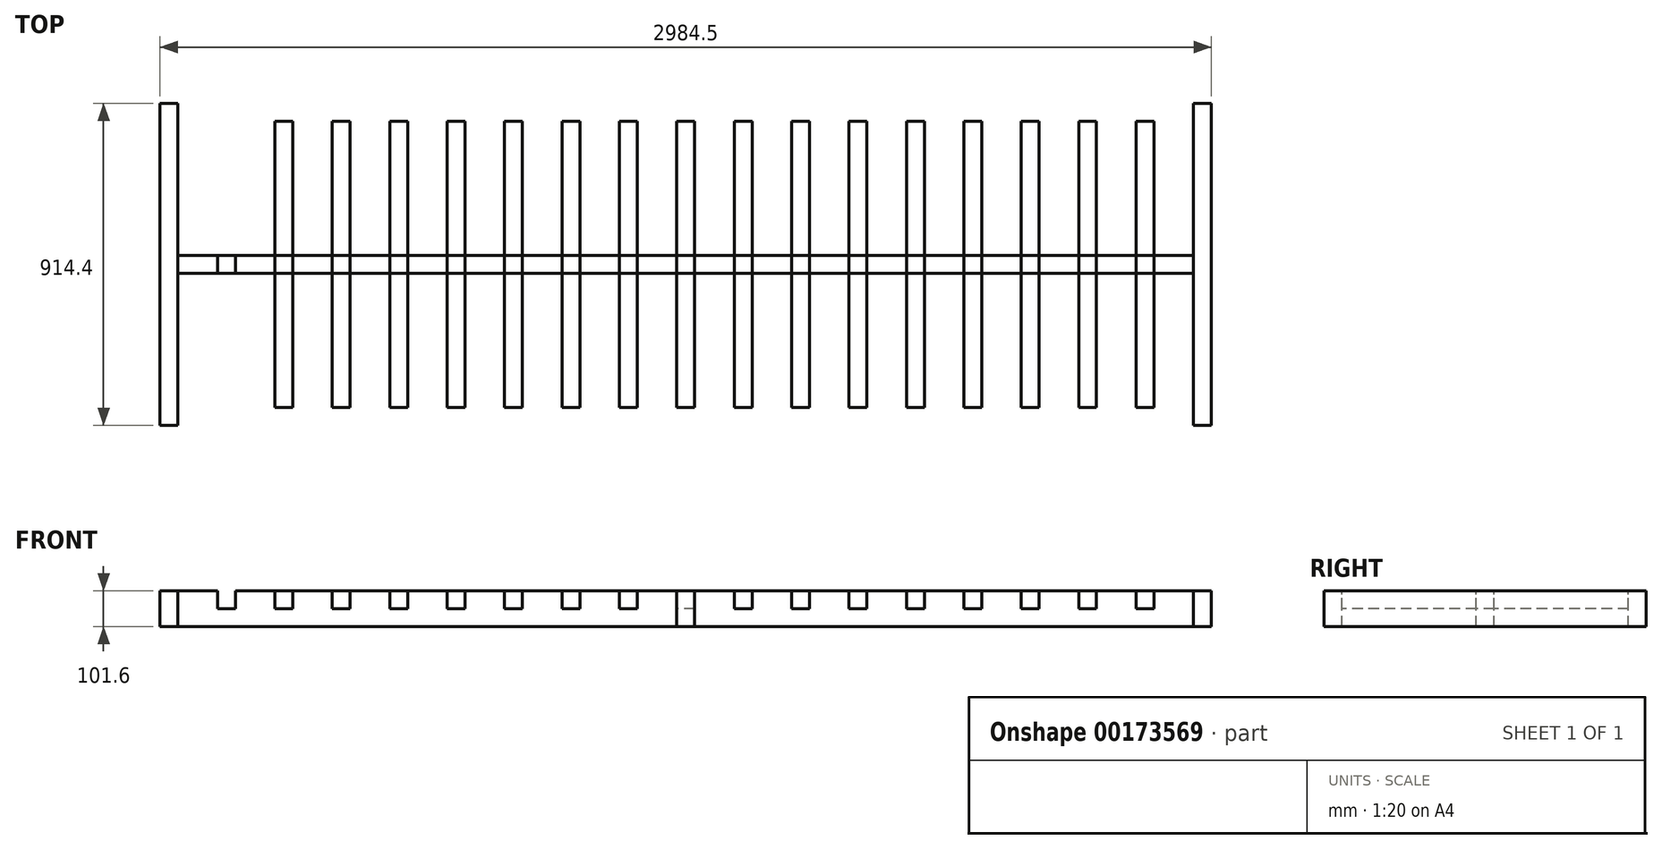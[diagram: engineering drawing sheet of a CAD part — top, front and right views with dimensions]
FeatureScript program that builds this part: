
annotation { "Feature Type Name" : "Feature", "Feature Type Description" : "" }
export const myFeature = defineFeature(function(context is Context, id is Id, definition is map)
    precondition{}
    {
        {
            var Q0;
            Q0=qCreatedBy(makeId("Top.planeOp"),FACE);
            var sketch = newSketch(context, id + "F0", { "sketchPlane" : qUnion([Q0])});
            skLineSegment(sketch, "E0.bottom", {"start": v(1492.25, 457.2) * mm, "end": v(-1492.25, 457.2) * mm});
            skLineSegment(sketch, "E0.top", {"start": v(1492.25, -457.2) * mm, "end": v(-1492.25, -457.2) * mm});
            skLineSegment(sketch, "E0.left", {"start": v(1492.25, 457.2) * mm, "end": v(1492.25, -457.2) * mm});
            skLineSegment(sketch, "E0.right", {"start": v(-1492.25, 457.2) * mm, "end": v(-1492.25, -457.2) * mm});
            skPoint(sketch, "E0.middle", {"position": v(0, 0) * mm});
            skLineSegment(sketch, "E1.0", {"start": v(1441.45, 406.4) * mm, "end": v(-1441.45, 406.4) * mm});
            skLineSegment(sketch, "E1.1", {"start": v(1441.45, 406.4) * mm, "end": v(1441.45, -406.4) * mm});
            skLineSegment(sketch, "E1.2", {"start": v(1441.45, -406.4) * mm, "end": v(-1441.45, -406.4) * mm});
            skLineSegment(sketch, "E1.3", {"start": v(-1441.45, 406.4) * mm, "end": v(-1441.45, -406.4) * mm});
            skLineSegment(sketch, "E2.bottom", {"start": v(1441.45, 25.4) * mm, "end": v(-1441.45, 25.4) * mm});
            skLineSegment(sketch, "E2.top", {"start": v(1441.45, -25.4) * mm, "end": v(-1441.45, -25.4) * mm});
            skLineSegment(sketch, "E2.left", {"start": v(1441.45, 25.4) * mm, "end": v(1441.45, -25.4) * mm});
            skLineSegment(sketch, "E2.right", {"start": v(-1441.45, 25.4) * mm, "end": v(-1441.45, -25.4) * mm});
            skLineSegment(sketch, "E3.bottom", {"start": v(-1329.18, 406.4) * mm, "end": v(-1278.38, 406.4) * mm});
            skLineSegment(sketch, "E3.top", {"start": v(-1329.18, -406.4) * mm, "end": v(-1278.38, -406.4) * mm});
            skLineSegment(sketch, "E3.left", {"start": v(-1329.18, 406.4) * mm, "end": v(-1329.18, -406.4) * mm});
            skLineSegment(sketch, "E3.right", {"start": v(-1278.38, 406.4) * mm, "end": v(-1278.38, -406.4) * mm});
            skLineSegment(sketch, "E4.1.0.0", {"start": v(-1115.4, 406.4) * mm, "end": v(-1115.4, -406.4) * mm});
            skLineSegment(sketch, "E4.1.0.1", {"start": v(-1166.2, 406.4) * mm, "end": v(-1166.2, -406.4) * mm});
            skLineSegment(sketch, "E4.2.0.0", {"start": v(-952.44, 406.4) * mm, "end": v(-952.44, -406.4) * mm});
            skLineSegment(sketch, "E4.2.0.1", {"start": v(-1003.24, 406.4) * mm, "end": v(-1003.24, -406.4) * mm});
            skLineSegment(sketch, "E4.direction1", {"start": v(-1278.38, -406.4) * mm, "end": v(-1115.4, -406.4) * mm, "construction": true});
            skLineSegment(sketch, "E5.0.3.0", {"start": v(-789.46, 406.4) * mm, "end": v(-789.46, -406.4) * mm});
            skLineSegment(sketch, "E5.3.3.0", {"start": v(-840.26, 406.4) * mm, "end": v(-840.26, -406.4) * mm});
            skLineSegment(sketch, "E5.0.4.0", {"start": v(-626.5, 406.4) * mm, "end": v(-626.5, -406.4) * mm});
            skLineSegment(sketch, "E5.3.4.0", {"start": v(-677.3, 406.4) * mm, "end": v(-677.3, -406.4) * mm});
            skLineSegment(sketch, "E5.0.5.0", {"start": v(-463.52, 406.4) * mm, "end": v(-463.52, -406.4) * mm});
            skLineSegment(sketch, "E5.3.5.0", {"start": v(-514.32, 406.4) * mm, "end": v(-514.32, -406.4) * mm});
            skLineSegment(sketch, "E5.0.6.0", {"start": v(-300.55, 406.4) * mm, "end": v(-300.55, -406.4) * mm});
            skLineSegment(sketch, "E5.3.6.0", {"start": v(-351.35, 406.4) * mm, "end": v(-351.35, -406.4) * mm});
            skLineSegment(sketch, "E5.0.7.0", {"start": v(-137.57, 406.4) * mm, "end": v(-137.57, -406.4) * mm});
            skLineSegment(sketch, "E5.3.7.0", {"start": v(-188.37, 406.4) * mm, "end": v(-188.37, -406.4) * mm});
            skLineSegment(sketch, "E5.0.8.0", {"start": v(25.4, 406.4) * mm, "end": v(25.4, -406.4) * mm});
            skLineSegment(sketch, "E5.3.8.0", {"start": v(-25.4, 406.4) * mm, "end": v(-25.4, -406.4) * mm});
            skLineSegment(sketch, "E5.0.9.0", {"start": v(188.37, 406.4) * mm, "end": v(188.37, -406.4) * mm});
            skLineSegment(sketch, "E5.3.9.0", {"start": v(137.57, 406.4) * mm, "end": v(137.57, -406.4) * mm});
            skLineSegment(sketch, "E5.0.10.0", {"start": v(351.35, 406.4) * mm, "end": v(351.35, -406.4) * mm});
            skLineSegment(sketch, "E5.3.10.0", {"start": v(300.55, 406.4) * mm, "end": v(300.55, -406.4) * mm});
            skLineSegment(sketch, "E5.0.11.0", {"start": v(514.32, 406.4) * mm, "end": v(514.32, -406.4) * mm});
            skLineSegment(sketch, "E5.3.11.0", {"start": v(463.52, 406.4) * mm, "end": v(463.52, -406.4) * mm});
            skLineSegment(sketch, "E6.0.12.0", {"start": v(677.3, 406.4) * mm, "end": v(677.3, -406.4) * mm});
            skLineSegment(sketch, "E6.3.12.0", {"start": v(626.5, 406.4) * mm, "end": v(626.5, -406.4) * mm});
            skLineSegment(sketch, "E6.0.13.0", {"start": v(840.26, 406.4) * mm, "end": v(840.26, -406.4) * mm});
            skLineSegment(sketch, "E6.3.13.0", {"start": v(789.46, 406.4) * mm, "end": v(789.46, -406.4) * mm});
            skLineSegment(sketch, "E7.0.14.0", {"start": v(1003.24, 406.4) * mm, "end": v(1003.24, -406.4) * mm});
            skLineSegment(sketch, "E7.3.14.0", {"start": v(952.44, 406.4) * mm, "end": v(952.44, -406.4) * mm});
            skLineSegment(sketch, "E7.0.15.0", {"start": v(1166.2, 406.4) * mm, "end": v(1166.2, -406.4) * mm});
            skLineSegment(sketch, "E7.3.15.0", {"start": v(1115.4, 406.4) * mm, "end": v(1115.4, -406.4) * mm});
            skLineSegment(sketch, "E8", {"start": v(-1441.45, 406.4) * mm, "end": v(-1441.45, 457.2) * mm});
            skLineSegment(sketch, "E9", {"start": v(-1441.45, -406.4) * mm, "end": v(-1441.45, -457.2) * mm});
            skLineSegment(sketch, "E10", {"start": v(1441.45, 406.4) * mm, "end": v(1441.45, 457.2) * mm});
            skLineSegment(sketch, "E11", {"start": v(1441.45, -406.4) * mm, "end": v(1441.45, -457.2) * mm});
            skLineSegment(sketch, "E12.0.16.0", {"start": v(1329.18, 406.4) * mm, "end": v(1329.18, -406.4) * mm});
            skLineSegment(sketch, "E12.3.16.0", {"start": v(1278.38, 406.4) * mm, "end": v(1278.38, -406.4) * mm});
            skSolve(sketch);
        }
        {
            var Q0;
            {var subQ0=sQuery(id+"F0.wireOp",EDGE,"E12.0.16.0");var subQ1=sQuery(id+"F0.wireOp",EDGE,"E1.0");var subQ2=makeQuery(id+"F0.imprint","INTERSECT",VERTEX,{"derivedFrom":[subQ1,subQ0]});Q0=makeQuery(id+"F0.imprint","IMPRINT",FACE,{"disambiguationData":[TD([[makeQuery(id+"F0.imprint","IMPRINT",EDGE,{"disambiguationData":[TD([[subQ2,-1.0]])],"derivedFrom":subQ1}),1.0]])]});}
            var Q1;
            {var subQ0=sQuery(id+"F0.wireOp",EDGE,"E12.0.16.0");var subQ1=sQuery(id+"F0.wireOp",EDGE,"E1.2");var subQ2=makeQuery(id+"F0.imprint","INTERSECT",VERTEX,{"derivedFrom":[subQ1,subQ0]});Q1=makeQuery(id+"F0.imprint","IMPRINT",FACE,{"disambiguationData":[TD([[makeQuery(id+"F0.imprint","IMPRINT",EDGE,{"disambiguationData":[TD([[subQ2,-1.0]])],"derivedFrom":subQ1}),-1.0]])]});}
            var Q2;
            {var subQ0=sQuery(id+"F0.wireOp",EDGE,"E7.0.15.0");var subQ1=sQuery(id+"F0.wireOp",EDGE,"E1.2");var subQ2=makeQuery(id+"F0.imprint","INTERSECT",VERTEX,{"derivedFrom":[subQ1,subQ0]});Q2=makeQuery(id+"F0.imprint","IMPRINT",FACE,{"disambiguationData":[TD([[makeQuery(id+"F0.imprint","IMPRINT",EDGE,{"disambiguationData":[TD([[subQ2,-1.0]])],"derivedFrom":subQ1}),-1.0]])]});}
            var Q3;
            {var subQ0=sQuery(id+"F0.wireOp",EDGE,"E7.0.15.0");var subQ1=sQuery(id+"F0.wireOp",EDGE,"E2.bottom");var subQ2=makeQuery(id+"F0.imprint","INTERSECT",VERTEX,{"derivedFrom":[subQ1,subQ0]});Q3=makeQuery(id+"F0.imprint","IMPRINT",FACE,{"disambiguationData":[TD([[makeQuery(id+"F0.imprint","IMPRINT",EDGE,{"disambiguationData":[TD([[subQ2,-1.0]])],"derivedFrom":subQ1}),1.0]])]});}
            var Q4;
            {var subQ0=sQuery(id+"F0.wireOp",EDGE,"E7.0.15.0");var subQ1=sQuery(id+"F0.wireOp",EDGE,"E1.0");var subQ2=makeQuery(id+"F0.imprint","INTERSECT",VERTEX,{"derivedFrom":[subQ1,subQ0]});Q4=makeQuery(id+"F0.imprint","IMPRINT",FACE,{"disambiguationData":[TD([[makeQuery(id+"F0.imprint","IMPRINT",EDGE,{"disambiguationData":[TD([[subQ2,-1.0]])],"derivedFrom":subQ1}),1.0]])]});}
            var Q5;
            {var subQ0=sQuery(id+"F0.wireOp",EDGE,"E7.0.14.0");var subQ1=sQuery(id+"F0.wireOp",EDGE,"E1.2");var subQ2=makeQuery(id+"F0.imprint","INTERSECT",VERTEX,{"derivedFrom":[subQ1,subQ0]});Q5=makeQuery(id+"F0.imprint","IMPRINT",FACE,{"disambiguationData":[TD([[makeQuery(id+"F0.imprint","IMPRINT",EDGE,{"disambiguationData":[TD([[subQ2,-1.0]])],"derivedFrom":subQ1}),-1.0]])]});}
            var Q6;
            {var subQ0=sQuery(id+"F0.wireOp",EDGE,"E7.0.14.0");var subQ1=sQuery(id+"F0.wireOp",EDGE,"E2.bottom");var subQ2=makeQuery(id+"F0.imprint","INTERSECT",VERTEX,{"derivedFrom":[subQ1,subQ0]});Q6=makeQuery(id+"F0.imprint","IMPRINT",FACE,{"disambiguationData":[TD([[makeQuery(id+"F0.imprint","IMPRINT",EDGE,{"disambiguationData":[TD([[subQ2,-1.0]])],"derivedFrom":subQ1}),1.0]])]});}
            var Q7;
            {var subQ0=sQuery(id+"F0.wireOp",EDGE,"E7.0.14.0");var subQ1=sQuery(id+"F0.wireOp",EDGE,"E1.0");var subQ2=makeQuery(id+"F0.imprint","INTERSECT",VERTEX,{"derivedFrom":[subQ1,subQ0]});Q7=makeQuery(id+"F0.imprint","IMPRINT",FACE,{"disambiguationData":[TD([[makeQuery(id+"F0.imprint","IMPRINT",EDGE,{"disambiguationData":[TD([[subQ2,-1.0]])],"derivedFrom":subQ1}),1.0]])]});}
            var Q8;
            {var subQ0=sQuery(id+"F0.wireOp",EDGE,"E6.0.12.0");var subQ1=sQuery(id+"F0.wireOp",EDGE,"E2.bottom");var subQ2=makeQuery(id+"F0.imprint","INTERSECT",VERTEX,{"derivedFrom":[subQ1,subQ0]});Q8=makeQuery(id+"F0.imprint","IMPRINT",FACE,{"disambiguationData":[TD([[makeQuery(id+"F0.imprint","IMPRINT",EDGE,{"disambiguationData":[TD([[subQ2,-1.0]])],"derivedFrom":subQ1}),1.0]])]});}
            var Q9;
            {var subQ0=sQuery(id+"F0.wireOp",EDGE,"E6.0.12.0");var subQ1=sQuery(id+"F0.wireOp",EDGE,"E1.0");var subQ2=makeQuery(id+"F0.imprint","INTERSECT",VERTEX,{"derivedFrom":[subQ1,subQ0]});Q9=makeQuery(id+"F0.imprint","IMPRINT",FACE,{"disambiguationData":[TD([[makeQuery(id+"F0.imprint","IMPRINT",EDGE,{"disambiguationData":[TD([[subQ2,-1.0]])],"derivedFrom":subQ1}),1.0]])]});}
            var Q10;
            {var subQ0=sQuery(id+"F0.wireOp",EDGE,"E6.0.12.0");var subQ1=sQuery(id+"F0.wireOp",EDGE,"E1.2");var subQ2=makeQuery(id+"F0.imprint","INTERSECT",VERTEX,{"derivedFrom":[subQ1,subQ0]});Q10=makeQuery(id+"F0.imprint","IMPRINT",FACE,{"disambiguationData":[TD([[makeQuery(id+"F0.imprint","IMPRINT",EDGE,{"disambiguationData":[TD([[subQ2,-1.0]])],"derivedFrom":subQ1}),-1.0]])]});}
            var Q11;
            {var subQ0=sQuery(id+"F0.wireOp",EDGE,"E5.0.11.0");var subQ1=sQuery(id+"F0.wireOp",EDGE,"E2.bottom");var subQ2=makeQuery(id+"F0.imprint","INTERSECT",VERTEX,{"derivedFrom":[subQ1,subQ0]});Q11=makeQuery(id+"F0.imprint","IMPRINT",FACE,{"disambiguationData":[TD([[makeQuery(id+"F0.imprint","IMPRINT",EDGE,{"disambiguationData":[TD([[subQ2,-1.0]])],"derivedFrom":subQ1}),1.0]])]});}
            var Q12;
            {var subQ0=sQuery(id+"F0.wireOp",EDGE,"E5.0.11.0");var subQ1=sQuery(id+"F0.wireOp",EDGE,"E1.0");var subQ2=makeQuery(id+"F0.imprint","INTERSECT",VERTEX,{"derivedFrom":[subQ1,subQ0]});Q12=makeQuery(id+"F0.imprint","IMPRINT",FACE,{"disambiguationData":[TD([[makeQuery(id+"F0.imprint","IMPRINT",EDGE,{"disambiguationData":[TD([[subQ2,-1.0]])],"derivedFrom":subQ1}),1.0]])]});}
            var Q13;
            {var subQ0=sQuery(id+"F0.wireOp",EDGE,"E5.0.11.0");var subQ1=sQuery(id+"F0.wireOp",EDGE,"E1.2");var subQ2=makeQuery(id+"F0.imprint","INTERSECT",VERTEX,{"derivedFrom":[subQ1,subQ0]});Q13=makeQuery(id+"F0.imprint","IMPRINT",FACE,{"disambiguationData":[TD([[makeQuery(id+"F0.imprint","IMPRINT",EDGE,{"disambiguationData":[TD([[subQ2,-1.0]])],"derivedFrom":subQ1}),-1.0]])]});}
            var Q14;
            {var subQ0=sQuery(id+"F0.wireOp",EDGE,"E5.0.10.0");var subQ1=sQuery(id+"F0.wireOp",EDGE,"E2.bottom");var subQ2=makeQuery(id+"F0.imprint","INTERSECT",VERTEX,{"derivedFrom":[subQ1,subQ0]});Q14=makeQuery(id+"F0.imprint","IMPRINT",FACE,{"disambiguationData":[TD([[makeQuery(id+"F0.imprint","IMPRINT",EDGE,{"disambiguationData":[TD([[subQ2,-1.0]])],"derivedFrom":subQ1}),1.0]])]});}
            var Q15;
            {var subQ0=sQuery(id+"F0.wireOp",EDGE,"E5.0.10.0");var subQ1=sQuery(id+"F0.wireOp",EDGE,"E1.2");var subQ2=makeQuery(id+"F0.imprint","INTERSECT",VERTEX,{"derivedFrom":[subQ1,subQ0]});Q15=makeQuery(id+"F0.imprint","IMPRINT",FACE,{"disambiguationData":[TD([[makeQuery(id+"F0.imprint","IMPRINT",EDGE,{"disambiguationData":[TD([[subQ2,-1.0]])],"derivedFrom":subQ1}),-1.0]])]});}
            var Q16;
            {var subQ0=sQuery(id+"F0.wireOp",EDGE,"E5.0.10.0");var subQ1=sQuery(id+"F0.wireOp",EDGE,"E1.0");var subQ2=makeQuery(id+"F0.imprint","INTERSECT",VERTEX,{"derivedFrom":[subQ1,subQ0]});Q16=makeQuery(id+"F0.imprint","IMPRINT",FACE,{"disambiguationData":[TD([[makeQuery(id+"F0.imprint","IMPRINT",EDGE,{"disambiguationData":[TD([[subQ2,-1.0]])],"derivedFrom":subQ1}),1.0]])]});}
            var Q17;
            {var subQ0=sQuery(id+"F0.wireOp",EDGE,"E5.0.9.0");var subQ1=sQuery(id+"F0.wireOp",EDGE,"E1.2");var subQ2=makeQuery(id+"F0.imprint","INTERSECT",VERTEX,{"derivedFrom":[subQ1,subQ0]});Q17=makeQuery(id+"F0.imprint","IMPRINT",FACE,{"disambiguationData":[TD([[makeQuery(id+"F0.imprint","IMPRINT",EDGE,{"disambiguationData":[TD([[subQ2,-1.0]])],"derivedFrom":subQ1}),-1.0]])]});}
            var Q18;
            {var subQ0=sQuery(id+"F0.wireOp",EDGE,"E5.0.9.0");var subQ1=sQuery(id+"F0.wireOp",EDGE,"E1.0");var subQ2=makeQuery(id+"F0.imprint","INTERSECT",VERTEX,{"derivedFrom":[subQ1,subQ0]});Q18=makeQuery(id+"F0.imprint","IMPRINT",FACE,{"disambiguationData":[TD([[makeQuery(id+"F0.imprint","IMPRINT",EDGE,{"disambiguationData":[TD([[subQ2,-1.0]])],"derivedFrom":subQ1}),1.0]])]});}
            var Q19;
            {var subQ0=sQuery(id+"F0.wireOp",EDGE,"E5.0.9.0");var subQ1=sQuery(id+"F0.wireOp",EDGE,"E2.bottom");var subQ2=makeQuery(id+"F0.imprint","INTERSECT",VERTEX,{"derivedFrom":[subQ1,subQ0]});Q19=makeQuery(id+"F0.imprint","IMPRINT",FACE,{"disambiguationData":[TD([[makeQuery(id+"F0.imprint","IMPRINT",EDGE,{"disambiguationData":[TD([[subQ2,-1.0]])],"derivedFrom":subQ1}),1.0]])]});}
            var Q20;
            {var subQ0=sQuery(id+"F0.wireOp",EDGE,"E5.0.8.0");var subQ1=sQuery(id+"F0.wireOp",EDGE,"E1.0");var subQ2=makeQuery(id+"F0.imprint","INTERSECT",VERTEX,{"derivedFrom":[subQ1,subQ0]});Q20=makeQuery(id+"F0.imprint","IMPRINT",FACE,{"disambiguationData":[TD([[makeQuery(id+"F0.imprint","IMPRINT",EDGE,{"disambiguationData":[TD([[subQ2,-1.0]])],"derivedFrom":subQ1}),1.0]])]});}
            var Q21;
            {var subQ0=sQuery(id+"F0.wireOp",EDGE,"E5.0.8.0");var subQ1=sQuery(id+"F0.wireOp",EDGE,"E1.2");var subQ2=makeQuery(id+"F0.imprint","INTERSECT",VERTEX,{"derivedFrom":[subQ1,subQ0]});Q21=makeQuery(id+"F0.imprint","IMPRINT",FACE,{"disambiguationData":[TD([[makeQuery(id+"F0.imprint","IMPRINT",EDGE,{"disambiguationData":[TD([[subQ2,-1.0]])],"derivedFrom":subQ1}),-1.0]])]});}
            var Q22;
            {var subQ0=sQuery(id+"F0.wireOp",EDGE,"E5.0.8.0");var subQ1=sQuery(id+"F0.wireOp",EDGE,"E2.bottom");var subQ2=makeQuery(id+"F0.imprint","INTERSECT",VERTEX,{"derivedFrom":[subQ1,subQ0]});Q22=makeQuery(id+"F0.imprint","IMPRINT",FACE,{"disambiguationData":[TD([[makeQuery(id+"F0.imprint","IMPRINT",EDGE,{"disambiguationData":[TD([[subQ2,-1.0]])],"derivedFrom":subQ1}),1.0]])]});}
            var Q23;
            {var subQ0=sQuery(id+"F0.wireOp",EDGE,"E5.0.7.0");var subQ1=sQuery(id+"F0.wireOp",EDGE,"E1.2");var subQ2=makeQuery(id+"F0.imprint","INTERSECT",VERTEX,{"derivedFrom":[subQ1,subQ0]});Q23=makeQuery(id+"F0.imprint","IMPRINT",FACE,{"disambiguationData":[TD([[makeQuery(id+"F0.imprint","IMPRINT",EDGE,{"disambiguationData":[TD([[subQ2,-1.0]])],"derivedFrom":subQ1}),-1.0]])]});}
            var Q24;
            {var subQ0=sQuery(id+"F0.wireOp",EDGE,"E5.0.7.0");var subQ1=sQuery(id+"F0.wireOp",EDGE,"E2.bottom");var subQ2=makeQuery(id+"F0.imprint","INTERSECT",VERTEX,{"derivedFrom":[subQ1,subQ0]});Q24=makeQuery(id+"F0.imprint","IMPRINT",FACE,{"disambiguationData":[TD([[makeQuery(id+"F0.imprint","IMPRINT",EDGE,{"disambiguationData":[TD([[subQ2,-1.0]])],"derivedFrom":subQ1}),1.0]])]});}
            var Q25;
            {var subQ0=sQuery(id+"F0.wireOp",EDGE,"E5.0.7.0");var subQ1=sQuery(id+"F0.wireOp",EDGE,"E1.0");var subQ2=makeQuery(id+"F0.imprint","INTERSECT",VERTEX,{"derivedFrom":[subQ1,subQ0]});Q25=makeQuery(id+"F0.imprint","IMPRINT",FACE,{"disambiguationData":[TD([[makeQuery(id+"F0.imprint","IMPRINT",EDGE,{"disambiguationData":[TD([[subQ2,-1.0]])],"derivedFrom":subQ1}),1.0]])]});}
            var Q26;
            {var subQ0=sQuery(id+"F0.wireOp",EDGE,"E5.0.5.0");var subQ1=sQuery(id+"F0.wireOp",EDGE,"E1.2");var subQ2=makeQuery(id+"F0.imprint","INTERSECT",VERTEX,{"derivedFrom":[subQ1,subQ0]});Q26=makeQuery(id+"F0.imprint","IMPRINT",FACE,{"disambiguationData":[TD([[makeQuery(id+"F0.imprint","IMPRINT",EDGE,{"disambiguationData":[TD([[subQ2,-1.0]])],"derivedFrom":subQ1}),-1.0]])]});}
            var Q27;
            {var subQ0=sQuery(id+"F0.wireOp",EDGE,"E5.0.5.0");var subQ1=sQuery(id+"F0.wireOp",EDGE,"E1.0");var subQ2=makeQuery(id+"F0.imprint","INTERSECT",VERTEX,{"derivedFrom":[subQ1,subQ0]});Q27=makeQuery(id+"F0.imprint","IMPRINT",FACE,{"disambiguationData":[TD([[makeQuery(id+"F0.imprint","IMPRINT",EDGE,{"disambiguationData":[TD([[subQ2,-1.0]])],"derivedFrom":subQ1}),1.0]])]});}
            var Q28;
            {var subQ0=sQuery(id+"F0.wireOp",EDGE,"E5.0.5.0");var subQ1=sQuery(id+"F0.wireOp",EDGE,"E2.bottom");var subQ2=makeQuery(id+"F0.imprint","INTERSECT",VERTEX,{"derivedFrom":[subQ1,subQ0]});Q28=makeQuery(id+"F0.imprint","IMPRINT",FACE,{"disambiguationData":[TD([[makeQuery(id+"F0.imprint","IMPRINT",EDGE,{"disambiguationData":[TD([[subQ2,-1.0]])],"derivedFrom":subQ1}),1.0]])]});}
            var Q29;
            {var subQ0=sQuery(id+"F0.wireOp",EDGE,"E5.0.3.0");var subQ1=sQuery(id+"F0.wireOp",EDGE,"E2.bottom");var subQ2=makeQuery(id+"F0.imprint","INTERSECT",VERTEX,{"derivedFrom":[subQ1,subQ0]});Q29=makeQuery(id+"F0.imprint","IMPRINT",FACE,{"disambiguationData":[TD([[makeQuery(id+"F0.imprint","IMPRINT",EDGE,{"disambiguationData":[TD([[subQ2,-1.0]])],"derivedFrom":subQ1}),1.0]])]});}
            var Q30;
            {var subQ0=sQuery(id+"F0.wireOp",EDGE,"E5.0.3.0");var subQ1=sQuery(id+"F0.wireOp",EDGE,"E1.2");var subQ2=makeQuery(id+"F0.imprint","INTERSECT",VERTEX,{"derivedFrom":[subQ1,subQ0]});Q30=makeQuery(id+"F0.imprint","IMPRINT",FACE,{"disambiguationData":[TD([[makeQuery(id+"F0.imprint","IMPRINT",EDGE,{"disambiguationData":[TD([[subQ2,-1.0]])],"derivedFrom":subQ1}),-1.0]])]});}
            var Q31;
            {var subQ0=sQuery(id+"F0.wireOp",EDGE,"E5.0.3.0");var subQ1=sQuery(id+"F0.wireOp",EDGE,"E1.0");var subQ2=makeQuery(id+"F0.imprint","INTERSECT",VERTEX,{"derivedFrom":[subQ1,subQ0]});Q31=makeQuery(id+"F0.imprint","IMPRINT",FACE,{"disambiguationData":[TD([[makeQuery(id+"F0.imprint","IMPRINT",EDGE,{"disambiguationData":[TD([[subQ2,-1.0]])],"derivedFrom":subQ1}),1.0]])]});}
            var Q32;
            {var subQ0=sQuery(id+"F0.wireOp",EDGE,"E4.2.0.0");var subQ1=sQuery(id+"F0.wireOp",EDGE,"E1.2");var subQ2=makeQuery(id+"F0.imprint","INTERSECT",VERTEX,{"derivedFrom":[subQ1,subQ0]});Q32=makeQuery(id+"F0.imprint","IMPRINT",FACE,{"disambiguationData":[TD([[makeQuery(id+"F0.imprint","IMPRINT",EDGE,{"disambiguationData":[TD([[subQ2,-1.0]])],"derivedFrom":subQ1}),-1.0]])]});}
            var Q33;
            {var subQ0=sQuery(id+"F0.wireOp",EDGE,"E4.2.0.0");var subQ1=sQuery(id+"F0.wireOp",EDGE,"E1.0");var subQ2=makeQuery(id+"F0.imprint","INTERSECT",VERTEX,{"derivedFrom":[subQ1,subQ0]});Q33=makeQuery(id+"F0.imprint","IMPRINT",FACE,{"disambiguationData":[TD([[makeQuery(id+"F0.imprint","IMPRINT",EDGE,{"disambiguationData":[TD([[subQ2,-1.0]])],"derivedFrom":subQ1}),1.0]])]});}
            var Q34;
            {var subQ0=sQuery(id+"F0.wireOp",EDGE,"E4.2.0.0");var subQ1=sQuery(id+"F0.wireOp",EDGE,"E2.bottom");var subQ2=makeQuery(id+"F0.imprint","INTERSECT",VERTEX,{"derivedFrom":[subQ1,subQ0]});Q34=makeQuery(id+"F0.imprint","IMPRINT",FACE,{"disambiguationData":[TD([[makeQuery(id+"F0.imprint","IMPRINT",EDGE,{"disambiguationData":[TD([[subQ2,-1.0]])],"derivedFrom":subQ1}),1.0]])]});}
            var Q35;
            {var subQ0=sQuery(id+"F0.wireOp",EDGE,"E4.1.0.0");var subQ1=sQuery(id+"F0.wireOp",EDGE,"E1.2");var subQ2=makeQuery(id+"F0.imprint","INTERSECT",VERTEX,{"derivedFrom":[subQ1,subQ0]});Q35=makeQuery(id+"F0.imprint","IMPRINT",FACE,{"disambiguationData":[TD([[makeQuery(id+"F0.imprint","IMPRINT",EDGE,{"disambiguationData":[TD([[subQ2,-1.0]])],"derivedFrom":subQ1}),-1.0]])]});}
            var Q36;
            {var subQ0=sQuery(id+"F0.wireOp",EDGE,"E12.0.16.0");var subQ1=sQuery(id+"F0.wireOp",EDGE,"E2.bottom");var subQ2=makeQuery(id+"F0.imprint","INTERSECT",VERTEX,{"derivedFrom":[subQ1,subQ0]});Q36=makeQuery(id+"F0.imprint","IMPRINT",FACE,{"disambiguationData":[TD([[makeQuery(id+"F0.imprint","IMPRINT",EDGE,{"disambiguationData":[TD([[subQ2,-1.0]])],"derivedFrom":subQ1}),1.0]])]});}
            var Q37;
            {var subQ5=sQuery(id+"F0.wireOp",EDGE,"E3.top");Q37=makeQuery(id+"F0.imprint","IMPRINT",FACE,{"disambiguationData":[TD([[makeQuery(id+"F0.imprint","IMPRINT",EDGE,{"derivedFrom":subQ5}),1.0]])]});}
            var Q38;
            {var subQ0=sQuery(id+"F0.wireOp",EDGE,"E3.right");var subQ1=sQuery(id+"F0.wireOp",EDGE,"E2.bottom");var subQ2=makeQuery(id+"F0.imprint","INTERSECT",VERTEX,{"derivedFrom":[subQ1,subQ0]});Q38=makeQuery(id+"F0.imprint","IMPRINT",FACE,{"disambiguationData":[TD([[makeQuery(id+"F0.imprint","IMPRINT",EDGE,{"disambiguationData":[TD([[subQ2,-1.0]])],"derivedFrom":subQ1}),1.0]])]});}
            var Q39;
            {var subQ5=sQuery(id+"F0.wireOp",EDGE,"E3.bottom");Q39=makeQuery(id+"F0.imprint","IMPRINT",FACE,{"disambiguationData":[TD([[makeQuery(id+"F0.imprint","IMPRINT",EDGE,{"derivedFrom":subQ5}),-1.0]])]});}
            var Q40;
            {var subQ0=sQuery(id+"F0.wireOp",EDGE,"E5.0.6.0");var subQ1=sQuery(id+"F0.wireOp",EDGE,"E1.2");var subQ2=makeQuery(id+"F0.imprint","INTERSECT",VERTEX,{"derivedFrom":[subQ1,subQ0]});Q40=makeQuery(id+"F0.imprint","IMPRINT",FACE,{"disambiguationData":[TD([[makeQuery(id+"F0.imprint","IMPRINT",EDGE,{"disambiguationData":[TD([[subQ2,-1.0]])],"derivedFrom":subQ1}),-1.0]])]});}
            var Q41;
            {var subQ0=sQuery(id+"F0.wireOp",EDGE,"E5.0.6.0");var subQ1=sQuery(id+"F0.wireOp",EDGE,"E2.bottom");var subQ2=makeQuery(id+"F0.imprint","INTERSECT",VERTEX,{"derivedFrom":[subQ1,subQ0]});Q41=makeQuery(id+"F0.imprint","IMPRINT",FACE,{"disambiguationData":[TD([[makeQuery(id+"F0.imprint","IMPRINT",EDGE,{"disambiguationData":[TD([[subQ2,-1.0]])],"derivedFrom":subQ1}),1.0]])]});}
            var Q42;
            {var subQ0=sQuery(id+"F0.wireOp",EDGE,"E5.0.6.0");var subQ1=sQuery(id+"F0.wireOp",EDGE,"E1.0");var subQ2=makeQuery(id+"F0.imprint","INTERSECT",VERTEX,{"derivedFrom":[subQ1,subQ0]});Q42=makeQuery(id+"F0.imprint","IMPRINT",FACE,{"disambiguationData":[TD([[makeQuery(id+"F0.imprint","IMPRINT",EDGE,{"disambiguationData":[TD([[subQ2,-1.0]])],"derivedFrom":subQ1}),1.0]])]});}
            var Q43;
            {var subQ0=sQuery(id+"F0.wireOp",EDGE,"E5.0.4.0");var subQ1=sQuery(id+"F0.wireOp",EDGE,"E1.2");var subQ2=makeQuery(id+"F0.imprint","INTERSECT",VERTEX,{"derivedFrom":[subQ1,subQ0]});Q43=makeQuery(id+"F0.imprint","IMPRINT",FACE,{"disambiguationData":[TD([[makeQuery(id+"F0.imprint","IMPRINT",EDGE,{"disambiguationData":[TD([[subQ2,-1.0]])],"derivedFrom":subQ1}),-1.0]])]});}
            var Q44;
            {var subQ0=sQuery(id+"F0.wireOp",EDGE,"E5.0.4.0");var subQ1=sQuery(id+"F0.wireOp",EDGE,"E1.0");var subQ2=makeQuery(id+"F0.imprint","INTERSECT",VERTEX,{"derivedFrom":[subQ1,subQ0]});Q44=makeQuery(id+"F0.imprint","IMPRINT",FACE,{"disambiguationData":[TD([[makeQuery(id+"F0.imprint","IMPRINT",EDGE,{"disambiguationData":[TD([[subQ2,-1.0]])],"derivedFrom":subQ1}),1.0]])]});}
            var Q45;
            {var subQ0=sQuery(id+"F0.wireOp",EDGE,"E5.0.4.0");var subQ1=sQuery(id+"F0.wireOp",EDGE,"E2.bottom");var subQ2=makeQuery(id+"F0.imprint","INTERSECT",VERTEX,{"derivedFrom":[subQ1,subQ0]});Q45=makeQuery(id+"F0.imprint","IMPRINT",FACE,{"disambiguationData":[TD([[makeQuery(id+"F0.imprint","IMPRINT",EDGE,{"disambiguationData":[TD([[subQ2,-1.0]])],"derivedFrom":subQ1}),1.0]])]});}
            var Q46;
            {var subQ0=sQuery(id+"F0.wireOp",EDGE,"E6.0.13.0");var subQ1=sQuery(id+"F0.wireOp",EDGE,"E1.2");var subQ2=makeQuery(id+"F0.imprint","INTERSECT",VERTEX,{"derivedFrom":[subQ1,subQ0]});Q46=makeQuery(id+"F0.imprint","IMPRINT",FACE,{"disambiguationData":[TD([[makeQuery(id+"F0.imprint","IMPRINT",EDGE,{"disambiguationData":[TD([[subQ2,-1.0]])],"derivedFrom":subQ1}),-1.0]])]});}
            var Q47;
            {var subQ0=sQuery(id+"F0.wireOp",EDGE,"E6.0.13.0");var subQ1=sQuery(id+"F0.wireOp",EDGE,"E1.0");var subQ2=makeQuery(id+"F0.imprint","INTERSECT",VERTEX,{"derivedFrom":[subQ1,subQ0]});Q47=makeQuery(id+"F0.imprint","IMPRINT",FACE,{"disambiguationData":[TD([[makeQuery(id+"F0.imprint","IMPRINT",EDGE,{"disambiguationData":[TD([[subQ2,-1.0]])],"derivedFrom":subQ1}),1.0]])]});}
            var Q48;
            {var subQ0=sQuery(id+"F0.wireOp",EDGE,"E6.0.13.0");var subQ1=sQuery(id+"F0.wireOp",EDGE,"E2.bottom");var subQ2=makeQuery(id+"F0.imprint","INTERSECT",VERTEX,{"derivedFrom":[subQ1,subQ0]});Q48=makeQuery(id+"F0.imprint","IMPRINT",FACE,{"disambiguationData":[TD([[makeQuery(id+"F0.imprint","IMPRINT",EDGE,{"disambiguationData":[TD([[subQ2,-1.0]])],"derivedFrom":subQ1}),1.0]])]});}
            var Q49;
            {var subQ0=sQuery(id+"F0.wireOp",EDGE,"E4.1.0.0");var subQ1=sQuery(id+"F0.wireOp",EDGE,"E1.0");var subQ2=makeQuery(id+"F0.imprint","INTERSECT",VERTEX,{"derivedFrom":[subQ1,subQ0]});Q49=makeQuery(id+"F0.imprint","IMPRINT",FACE,{"disambiguationData":[TD([[makeQuery(id+"F0.imprint","IMPRINT",EDGE,{"disambiguationData":[TD([[subQ2,-1.0]])],"derivedFrom":subQ1}),1.0]])]});}
            var Q50;
            {var subQ0=sQuery(id+"F0.wireOp",EDGE,"E4.1.0.0");var subQ1=sQuery(id+"F0.wireOp",EDGE,"E2.bottom");var subQ2=makeQuery(id+"F0.imprint","INTERSECT",VERTEX,{"derivedFrom":[subQ1,subQ0]});Q50=makeQuery(id+"F0.imprint","IMPRINT",FACE,{"disambiguationData":[TD([[makeQuery(id+"F0.imprint","IMPRINT",EDGE,{"disambiguationData":[TD([[subQ2,-1.0]])],"derivedFrom":subQ1}),1.0]])]});}
            extrude(context, id + "F1", {"entities" : qUnion([Q0, Q1, Q2, Q3, Q4, Q5, Q6, Q7, Q8, Q9, Q10, Q11, Q12, Q13, Q14, Q15, Q16, Q17, Q18, Q19, Q20, Q21, Q22, Q23, Q24, Q25, Q26, Q27, Q28, Q29, Q30, Q31, Q32, Q33, Q34, Q35, Q36, Q37, Q38, Q39, Q40, Q41, Q42, Q43, Q44, Q45, Q46, Q47, Q48, Q49, Q50]), "oppositeDirection" : true, "depth" : 50.8 * mm});
        }
        {
            var Q0;
            {var subQ0=sQuery(id+"F0.wireOp",EDGE,"E5.0.8.0");var subQ1=sQuery(id+"F0.wireOp",EDGE,"E1.0");var subQ2=makeQuery(id+"F0.imprint","INTERSECT",VERTEX,{"derivedFrom":[subQ1,subQ0]});Q0=makeQuery(id+"F0.imprint","IMPRINT",FACE,{"disambiguationData":[TD([[makeQuery(id+"F0.imprint","IMPRINT",EDGE,{"disambiguationData":[TD([[subQ2,-1.0]])],"derivedFrom":subQ1}),1.0]])]});}
            var Q1;
            {var subQ0=sQuery(id+"F0.wireOp",EDGE,"E5.0.8.0");var subQ1=sQuery(id+"F0.wireOp",EDGE,"E1.2");var subQ2=makeQuery(id+"F0.imprint","INTERSECT",VERTEX,{"derivedFrom":[subQ1,subQ0]});Q1=makeQuery(id+"F0.imprint","IMPRINT",FACE,{"disambiguationData":[TD([[makeQuery(id+"F0.imprint","IMPRINT",EDGE,{"disambiguationData":[TD([[subQ2,-1.0]])],"derivedFrom":subQ1}),-1.0]])]});}
            extrude(context, id + "F2", {"entities" : qUnion([Q0, Q1]), "operationType" : NewBodyOperationType.ADD, "oppositeDirection" : true, "depth" : 101.6 * mm});
        }
        {
            var Q0;
            {var subQ4=sQuery(id+"F0.wireOp",EDGE,"E0.right");Q0=makeQuery(id+"F0.imprint","IMPRINT",FACE,{"disambiguationData":[TD([[makeQuery(id+"F0.imprint","IMPRINT",EDGE,{"derivedFrom":subQ4}),1.0]])]});}
            var Q1;
            {var subQ3=sQuery(id+"F0.wireOp",EDGE,"E0.left");Q1=makeQuery(id+"F0.imprint","IMPRINT",FACE,{"disambiguationData":[TD([[makeQuery(id+"F0.imprint","IMPRINT",EDGE,{"derivedFrom":subQ3}),-1.0]])]});}
            extrude(context, id + "F3", {"entities" : qUnion([Q0, Q1]), "oppositeDirection" : true, "depth" : 101.6 * mm});
        }
        {
            var Q0;
            {var subQ0=sQuery(id+"F0.wireOp",EDGE,"E2.left");Q0=makeQuery(id+"F0.imprint","IMPRINT",FACE,{"disambiguationData":[TD([[makeQuery(id+"F0.imprint","IMPRINT",EDGE,{"derivedFrom":subQ0}),-1.0]])]});}
            var Q1;
            {var subQ0=sQuery(id+"F0.wireOp",EDGE,"f316c000-d505-4a66-956d-6f149d2779e3.0.17.0");var subQ1=sQuery(id+"F0.wireOp",EDGE,"E2.bottom");var subQ2=makeQuery(id+"F0.imprint","INTERSECT",VERTEX,{"derivedFrom":[subQ1,subQ0]});Q1=makeQuery(id+"F0.imprint","IMPRINT",FACE,{"disambiguationData":[TD([[makeQuery(id+"F0.imprint","IMPRINT",EDGE,{"disambiguationData":[TD([[subQ2,-1.0]])],"derivedFrom":subQ1}),1.0]])]});}
            var Q2;
            {var subQ0=sQuery(id+"F0.wireOp",EDGE,"f316c000-d505-4a66-956d-6f149d2779e3.3.17.0");var subQ1=sQuery(id+"F0.wireOp",EDGE,"E2.bottom");var subQ2=makeQuery(id+"F0.imprint","INTERSECT",VERTEX,{"derivedFrom":[subQ1,subQ0]});Q2=makeQuery(id+"F0.imprint","IMPRINT",FACE,{"disambiguationData":[TD([[makeQuery(id+"F0.imprint","IMPRINT",EDGE,{"disambiguationData":[TD([[subQ2,-1.0]])],"derivedFrom":subQ1}),1.0]])]});}
            var Q3;
            {var subQ0=sQuery(id+"F0.wireOp",EDGE,"f316c000-d505-4a66-956d-6f149d2779e3.0.16.0");var subQ1=sQuery(id+"F0.wireOp",EDGE,"E2.bottom");var subQ2=makeQuery(id+"F0.imprint","INTERSECT",VERTEX,{"derivedFrom":[subQ1,subQ0]});Q3=makeQuery(id+"F0.imprint","IMPRINT",FACE,{"disambiguationData":[TD([[makeQuery(id+"F0.imprint","IMPRINT",EDGE,{"disambiguationData":[TD([[subQ2,-1.0]])],"derivedFrom":subQ1}),1.0]])]});}
            var Q4;
            {var subQ0=sQuery(id+"F0.wireOp",EDGE,"f316c000-d505-4a66-956d-6f149d2779e3.3.16.0");var subQ1=sQuery(id+"F0.wireOp",EDGE,"E2.bottom");var subQ2=makeQuery(id+"F0.imprint","INTERSECT",VERTEX,{"derivedFrom":[subQ1,subQ0]});Q4=makeQuery(id+"F0.imprint","IMPRINT",FACE,{"disambiguationData":[TD([[makeQuery(id+"F0.imprint","IMPRINT",EDGE,{"disambiguationData":[TD([[subQ2,-1.0]])],"derivedFrom":subQ1}),1.0]])]});}
            var Q5;
            {var subQ0=sQuery(id+"F0.wireOp",EDGE,"E7.0.15.0");var subQ1=sQuery(id+"F0.wireOp",EDGE,"E2.bottom");var subQ2=makeQuery(id+"F0.imprint","INTERSECT",VERTEX,{"derivedFrom":[subQ1,subQ0]});Q5=makeQuery(id+"F0.imprint","IMPRINT",FACE,{"disambiguationData":[TD([[makeQuery(id+"F0.imprint","IMPRINT",EDGE,{"disambiguationData":[TD([[subQ2,-1.0]])],"derivedFrom":subQ1}),1.0]])]});}
            var Q6;
            {var subQ0=sQuery(id+"F0.wireOp",EDGE,"E7.0.14.0");var subQ1=sQuery(id+"F0.wireOp",EDGE,"E2.bottom");var subQ2=makeQuery(id+"F0.imprint","INTERSECT",VERTEX,{"derivedFrom":[subQ1,subQ0]});Q6=makeQuery(id+"F0.imprint","IMPRINT",FACE,{"disambiguationData":[TD([[makeQuery(id+"F0.imprint","IMPRINT",EDGE,{"disambiguationData":[TD([[subQ2,-1.0]])],"derivedFrom":subQ1}),1.0]])]});}
            var Q7;
            {var subQ0=sQuery(id+"F0.wireOp",EDGE,"E7.3.15.0");var subQ1=sQuery(id+"F0.wireOp",EDGE,"E2.bottom");var subQ2=makeQuery(id+"F0.imprint","INTERSECT",VERTEX,{"derivedFrom":[subQ1,subQ0]});Q7=makeQuery(id+"F0.imprint","IMPRINT",FACE,{"disambiguationData":[TD([[makeQuery(id+"F0.imprint","IMPRINT",EDGE,{"disambiguationData":[TD([[subQ2,-1.0]])],"derivedFrom":subQ1}),1.0]])]});}
            var Q8;
            {var subQ0=sQuery(id+"F0.wireOp",EDGE,"E7.3.14.0");var subQ1=sQuery(id+"F0.wireOp",EDGE,"E2.bottom");var subQ2=makeQuery(id+"F0.imprint","INTERSECT",VERTEX,{"derivedFrom":[subQ1,subQ0]});Q8=makeQuery(id+"F0.imprint","IMPRINT",FACE,{"disambiguationData":[TD([[makeQuery(id+"F0.imprint","IMPRINT",EDGE,{"disambiguationData":[TD([[subQ2,-1.0]])],"derivedFrom":subQ1}),1.0]])]});}
            var Q9;
            {var subQ0=sQuery(id+"F0.wireOp",EDGE,"E6.0.13.0");var subQ1=sQuery(id+"F0.wireOp",EDGE,"E2.bottom");var subQ2=makeQuery(id+"F0.imprint","INTERSECT",VERTEX,{"derivedFrom":[subQ1,subQ0]});Q9=makeQuery(id+"F0.imprint","IMPRINT",FACE,{"disambiguationData":[TD([[makeQuery(id+"F0.imprint","IMPRINT",EDGE,{"disambiguationData":[TD([[subQ2,-1.0]])],"derivedFrom":subQ1}),1.0]])]});}
            var Q10;
            {var subQ0=sQuery(id+"F0.wireOp",EDGE,"E6.3.12.0");var subQ1=sQuery(id+"F0.wireOp",EDGE,"E2.bottom");var subQ2=makeQuery(id+"F0.imprint","INTERSECT",VERTEX,{"derivedFrom":[subQ1,subQ0]});Q10=makeQuery(id+"F0.imprint","IMPRINT",FACE,{"disambiguationData":[TD([[makeQuery(id+"F0.imprint","IMPRINT",EDGE,{"disambiguationData":[TD([[subQ2,-1.0]])],"derivedFrom":subQ1}),1.0]])]});}
            var Q11;
            {var subQ0=sQuery(id+"F0.wireOp",EDGE,"E5.0.6.0");var subQ1=sQuery(id+"F0.wireOp",EDGE,"E2.bottom");var subQ2=makeQuery(id+"F0.imprint","INTERSECT",VERTEX,{"derivedFrom":[subQ1,subQ0]});Q11=makeQuery(id+"F0.imprint","IMPRINT",FACE,{"disambiguationData":[TD([[makeQuery(id+"F0.imprint","IMPRINT",EDGE,{"disambiguationData":[TD([[subQ2,-1.0]])],"derivedFrom":subQ1}),1.0]])]});}
            var Q12;
            {var subQ0=sQuery(id+"F0.wireOp",EDGE,"E5.0.10.0");var subQ1=sQuery(id+"F0.wireOp",EDGE,"E2.bottom");var subQ2=makeQuery(id+"F0.imprint","INTERSECT",VERTEX,{"derivedFrom":[subQ1,subQ0]});Q12=makeQuery(id+"F0.imprint","IMPRINT",FACE,{"disambiguationData":[TD([[makeQuery(id+"F0.imprint","IMPRINT",EDGE,{"disambiguationData":[TD([[subQ2,-1.0]])],"derivedFrom":subQ1}),1.0]])]});}
            var Q13;
            {var subQ0=sQuery(id+"F0.wireOp",EDGE,"E5.3.11.0");var subQ1=sQuery(id+"F0.wireOp",EDGE,"E2.bottom");var subQ2=makeQuery(id+"F0.imprint","INTERSECT",VERTEX,{"derivedFrom":[subQ1,subQ0]});Q13=makeQuery(id+"F0.imprint","IMPRINT",FACE,{"disambiguationData":[TD([[makeQuery(id+"F0.imprint","IMPRINT",EDGE,{"disambiguationData":[TD([[subQ2,-1.0]])],"derivedFrom":subQ1}),1.0]])]});}
            var Q14;
            {var subQ0=sQuery(id+"F0.wireOp",EDGE,"E6.0.12.0");var subQ1=sQuery(id+"F0.wireOp",EDGE,"E2.bottom");var subQ2=makeQuery(id+"F0.imprint","INTERSECT",VERTEX,{"derivedFrom":[subQ1,subQ0]});Q14=makeQuery(id+"F0.imprint","IMPRINT",FACE,{"disambiguationData":[TD([[makeQuery(id+"F0.imprint","IMPRINT",EDGE,{"disambiguationData":[TD([[subQ2,-1.0]])],"derivedFrom":subQ1}),1.0]])]});}
            var Q15;
            {var subQ0=sQuery(id+"F0.wireOp",EDGE,"E5.3.7.0");var subQ1=sQuery(id+"F0.wireOp",EDGE,"E2.bottom");var subQ2=makeQuery(id+"F0.imprint","INTERSECT",VERTEX,{"derivedFrom":[subQ1,subQ0]});Q15=makeQuery(id+"F0.imprint","IMPRINT",FACE,{"disambiguationData":[TD([[makeQuery(id+"F0.imprint","IMPRINT",EDGE,{"disambiguationData":[TD([[subQ2,-1.0]])],"derivedFrom":subQ1}),1.0]])]});}
            var Q16;
            {var subQ0=sQuery(id+"F0.wireOp",EDGE,"E5.3.3.0");var subQ1=sQuery(id+"F0.wireOp",EDGE,"E2.bottom");var subQ2=makeQuery(id+"F0.imprint","INTERSECT",VERTEX,{"derivedFrom":[subQ1,subQ0]});Q16=makeQuery(id+"F0.imprint","IMPRINT",FACE,{"disambiguationData":[TD([[makeQuery(id+"F0.imprint","IMPRINT",EDGE,{"disambiguationData":[TD([[subQ2,-1.0]])],"derivedFrom":subQ1}),1.0]])]});}
            var Q17;
            {var subQ0=sQuery(id+"F0.wireOp",EDGE,"E4.2.0.0");var subQ1=sQuery(id+"F0.wireOp",EDGE,"E2.bottom");var subQ2=makeQuery(id+"F0.imprint","INTERSECT",VERTEX,{"derivedFrom":[subQ1,subQ0]});Q17=makeQuery(id+"F0.imprint","IMPRINT",FACE,{"disambiguationData":[TD([[makeQuery(id+"F0.imprint","IMPRINT",EDGE,{"disambiguationData":[TD([[subQ2,-1.0]])],"derivedFrom":subQ1}),1.0]])]});}
            var Q18;
            {var subQ0=sQuery(id+"F0.wireOp",EDGE,"E4.1.0.1");var subQ1=sQuery(id+"F0.wireOp",EDGE,"E2.bottom");var subQ2=makeQuery(id+"F0.imprint","INTERSECT",VERTEX,{"derivedFrom":[subQ1,subQ0]});Q18=makeQuery(id+"F0.imprint","IMPRINT",FACE,{"disambiguationData":[TD([[makeQuery(id+"F0.imprint","IMPRINT",EDGE,{"disambiguationData":[TD([[subQ2,-1.0]])],"derivedFrom":subQ1}),1.0]])]});}
            var Q19;
            {var subQ0=sQuery(id+"F0.wireOp",EDGE,"E5.0.7.0");var subQ1=sQuery(id+"F0.wireOp",EDGE,"E2.bottom");var subQ2=makeQuery(id+"F0.imprint","INTERSECT",VERTEX,{"derivedFrom":[subQ1,subQ0]});Q19=makeQuery(id+"F0.imprint","IMPRINT",FACE,{"disambiguationData":[TD([[makeQuery(id+"F0.imprint","IMPRINT",EDGE,{"disambiguationData":[TD([[subQ2,-1.0]])],"derivedFrom":subQ1}),1.0]])]});}
            var Q20;
            {var subQ0=sQuery(id+"F0.wireOp",EDGE,"E5.3.9.0");var subQ1=sQuery(id+"F0.wireOp",EDGE,"E2.bottom");var subQ2=makeQuery(id+"F0.imprint","INTERSECT",VERTEX,{"derivedFrom":[subQ1,subQ0]});Q20=makeQuery(id+"F0.imprint","IMPRINT",FACE,{"disambiguationData":[TD([[makeQuery(id+"F0.imprint","IMPRINT",EDGE,{"disambiguationData":[TD([[subQ2,-1.0]])],"derivedFrom":subQ1}),1.0]])]});}
            var Q21;
            {var subQ0=sQuery(id+"F0.wireOp",EDGE,"E5.3.8.0");var subQ1=sQuery(id+"F0.wireOp",EDGE,"E2.bottom");var subQ2=makeQuery(id+"F0.imprint","INTERSECT",VERTEX,{"derivedFrom":[subQ1,subQ0]});Q21=makeQuery(id+"F0.imprint","IMPRINT",FACE,{"disambiguationData":[TD([[makeQuery(id+"F0.imprint","IMPRINT",EDGE,{"disambiguationData":[TD([[subQ2,-1.0]])],"derivedFrom":subQ1}),1.0]])]});}
            var Q22;
            {var subQ0=sQuery(id+"F0.wireOp",EDGE,"E4.2.0.1");var subQ1=sQuery(id+"F0.wireOp",EDGE,"E2.bottom");var subQ2=makeQuery(id+"F0.imprint","INTERSECT",VERTEX,{"derivedFrom":[subQ1,subQ0]});Q22=makeQuery(id+"F0.imprint","IMPRINT",FACE,{"disambiguationData":[TD([[makeQuery(id+"F0.imprint","IMPRINT",EDGE,{"disambiguationData":[TD([[subQ2,-1.0]])],"derivedFrom":subQ1}),1.0]])]});}
            var Q23;
            {var subQ0=sQuery(id+"F0.wireOp",EDGE,"E5.3.10.0");var subQ1=sQuery(id+"F0.wireOp",EDGE,"E2.bottom");var subQ2=makeQuery(id+"F0.imprint","INTERSECT",VERTEX,{"derivedFrom":[subQ1,subQ0]});Q23=makeQuery(id+"F0.imprint","IMPRINT",FACE,{"disambiguationData":[TD([[makeQuery(id+"F0.imprint","IMPRINT",EDGE,{"disambiguationData":[TD([[subQ2,-1.0]])],"derivedFrom":subQ1}),1.0]])]});}
            var Q24;
            {var subQ0=sQuery(id+"F0.wireOp",EDGE,"E2.right");Q24=makeQuery(id+"F0.imprint","IMPRINT",FACE,{"disambiguationData":[TD([[makeQuery(id+"F0.imprint","IMPRINT",EDGE,{"derivedFrom":subQ0}),1.0]])]});}
            var Q25;
            {var subQ0=sQuery(id+"F0.wireOp",EDGE,"E4.1.0.0");var subQ1=sQuery(id+"F0.wireOp",EDGE,"E2.bottom");var subQ2=makeQuery(id+"F0.imprint","INTERSECT",VERTEX,{"derivedFrom":[subQ1,subQ0]});Q25=makeQuery(id+"F0.imprint","IMPRINT",FACE,{"disambiguationData":[TD([[makeQuery(id+"F0.imprint","IMPRINT",EDGE,{"disambiguationData":[TD([[subQ2,-1.0]])],"derivedFrom":subQ1}),1.0]])]});}
            var Q26;
            {var subQ0=sQuery(id+"F0.wireOp",EDGE,"E5.0.9.0");var subQ1=sQuery(id+"F0.wireOp",EDGE,"E2.bottom");var subQ2=makeQuery(id+"F0.imprint","INTERSECT",VERTEX,{"derivedFrom":[subQ1,subQ0]});Q26=makeQuery(id+"F0.imprint","IMPRINT",FACE,{"disambiguationData":[TD([[makeQuery(id+"F0.imprint","IMPRINT",EDGE,{"disambiguationData":[TD([[subQ2,-1.0]])],"derivedFrom":subQ1}),1.0]])]});}
            var Q27;
            {var subQ0=sQuery(id+"F0.wireOp",EDGE,"E5.0.3.0");var subQ1=sQuery(id+"F0.wireOp",EDGE,"E2.bottom");var subQ2=makeQuery(id+"F0.imprint","INTERSECT",VERTEX,{"derivedFrom":[subQ1,subQ0]});Q27=makeQuery(id+"F0.imprint","IMPRINT",FACE,{"disambiguationData":[TD([[makeQuery(id+"F0.imprint","IMPRINT",EDGE,{"disambiguationData":[TD([[subQ2,-1.0]])],"derivedFrom":subQ1}),1.0]])]});}
            var Q28;
            {var subQ0=sQuery(id+"F0.wireOp",EDGE,"E5.0.8.0");var subQ1=sQuery(id+"F0.wireOp",EDGE,"E2.bottom");var subQ2=makeQuery(id+"F0.imprint","INTERSECT",VERTEX,{"derivedFrom":[subQ1,subQ0]});Q28=makeQuery(id+"F0.imprint","IMPRINT",FACE,{"disambiguationData":[TD([[makeQuery(id+"F0.imprint","IMPRINT",EDGE,{"disambiguationData":[TD([[subQ2,-1.0]])],"derivedFrom":subQ1}),1.0]])]});}
            var Q29;
            {var subQ0=sQuery(id+"F0.wireOp",EDGE,"E5.0.5.0");var subQ1=sQuery(id+"F0.wireOp",EDGE,"E2.bottom");var subQ2=makeQuery(id+"F0.imprint","INTERSECT",VERTEX,{"derivedFrom":[subQ1,subQ0]});Q29=makeQuery(id+"F0.imprint","IMPRINT",FACE,{"disambiguationData":[TD([[makeQuery(id+"F0.imprint","IMPRINT",EDGE,{"disambiguationData":[TD([[subQ2,-1.0]])],"derivedFrom":subQ1}),1.0]])]});}
            var Q30;
            {var subQ0=sQuery(id+"F0.wireOp",EDGE,"E5.3.6.0");var subQ1=sQuery(id+"F0.wireOp",EDGE,"E2.bottom");var subQ2=makeQuery(id+"F0.imprint","INTERSECT",VERTEX,{"derivedFrom":[subQ1,subQ0]});Q30=makeQuery(id+"F0.imprint","IMPRINT",FACE,{"disambiguationData":[TD([[makeQuery(id+"F0.imprint","IMPRINT",EDGE,{"disambiguationData":[TD([[subQ2,-1.0]])],"derivedFrom":subQ1}),1.0]])]});}
            var Q31;
            {var subQ0=sQuery(id+"F0.wireOp",EDGE,"E6.3.13.0");var subQ1=sQuery(id+"F0.wireOp",EDGE,"E2.bottom");var subQ2=makeQuery(id+"F0.imprint","INTERSECT",VERTEX,{"derivedFrom":[subQ1,subQ0]});Q31=makeQuery(id+"F0.imprint","IMPRINT",FACE,{"disambiguationData":[TD([[makeQuery(id+"F0.imprint","IMPRINT",EDGE,{"disambiguationData":[TD([[subQ2,-1.0]])],"derivedFrom":subQ1}),1.0]])]});}
            var Q32;
            {var subQ0=sQuery(id+"F0.wireOp",EDGE,"E3.right");var subQ1=sQuery(id+"F0.wireOp",EDGE,"E2.bottom");var subQ2=makeQuery(id+"F0.imprint","INTERSECT",VERTEX,{"derivedFrom":[subQ1,subQ0]});Q32=makeQuery(id+"F0.imprint","IMPRINT",FACE,{"disambiguationData":[TD([[makeQuery(id+"F0.imprint","IMPRINT",EDGE,{"disambiguationData":[TD([[subQ2,-1.0]])],"derivedFrom":subQ1}),1.0]])]});}
            var Q33;
            {var subQ0=sQuery(id+"F0.wireOp",EDGE,"E5.3.5.0");var subQ1=sQuery(id+"F0.wireOp",EDGE,"E2.bottom");var subQ2=makeQuery(id+"F0.imprint","INTERSECT",VERTEX,{"derivedFrom":[subQ1,subQ0]});Q33=makeQuery(id+"F0.imprint","IMPRINT",FACE,{"disambiguationData":[TD([[makeQuery(id+"F0.imprint","IMPRINT",EDGE,{"disambiguationData":[TD([[subQ2,-1.0]])],"derivedFrom":subQ1}),1.0]])]});}
            var Q34;
            {var subQ0=sQuery(id+"F0.wireOp",EDGE,"E5.3.4.0");var subQ1=sQuery(id+"F0.wireOp",EDGE,"E2.bottom");var subQ2=makeQuery(id+"F0.imprint","INTERSECT",VERTEX,{"derivedFrom":[subQ1,subQ0]});Q34=makeQuery(id+"F0.imprint","IMPRINT",FACE,{"disambiguationData":[TD([[makeQuery(id+"F0.imprint","IMPRINT",EDGE,{"disambiguationData":[TD([[subQ2,-1.0]])],"derivedFrom":subQ1}),1.0]])]});}
            var Q35;
            {var subQ0=sQuery(id+"F0.wireOp",EDGE,"E5.0.4.0");var subQ1=sQuery(id+"F0.wireOp",EDGE,"E2.bottom");var subQ2=makeQuery(id+"F0.imprint","INTERSECT",VERTEX,{"derivedFrom":[subQ1,subQ0]});Q35=makeQuery(id+"F0.imprint","IMPRINT",FACE,{"disambiguationData":[TD([[makeQuery(id+"F0.imprint","IMPRINT",EDGE,{"disambiguationData":[TD([[subQ2,-1.0]])],"derivedFrom":subQ1}),1.0]])]});}
            var Q36;
            {var subQ0=sQuery(id+"F0.wireOp",EDGE,"E5.0.11.0");var subQ1=sQuery(id+"F0.wireOp",EDGE,"E2.bottom");var subQ2=makeQuery(id+"F0.imprint","INTERSECT",VERTEX,{"derivedFrom":[subQ1,subQ0]});Q36=makeQuery(id+"F0.imprint","IMPRINT",FACE,{"disambiguationData":[TD([[makeQuery(id+"F0.imprint","IMPRINT",EDGE,{"disambiguationData":[TD([[subQ2,-1.0]])],"derivedFrom":subQ1}),1.0]])]});}
            var Q37;
            {var subQ38=sQuery(id+"F0.wireOp",EDGE,"E3.bottom");Q37=makeQuery(id+"F0.imprint","IMPRINT",FACE,{"disambiguationData":[TD([[makeQuery(id+"F0.imprint","IMPRINT",EDGE,{"derivedFrom":subQ38}),1.0]])]});}
            var Q38;
            {var subQ37=sQuery(id+"F0.wireOp",EDGE,"E3.top");Q38=makeQuery(id+"F0.imprint","IMPRINT",FACE,{"disambiguationData":[TD([[makeQuery(id+"F0.imprint","IMPRINT",EDGE,{"derivedFrom":subQ37}),-1.0]])]});}
            extrude(context, id + "F4", {"entities" : qUnion([Q0, Q1, Q2, Q3, Q4, Q5, Q6, Q7, Q8, Q9, Q10, Q11, Q12, Q13, Q14, Q15, Q16, Q17, Q18, Q19, Q20, Q21, Q22, Q23, Q24, Q25, Q26, Q27, Q28, Q29, Q30, Q31, Q32, Q33, Q34, Q35, Q36, Q37, Q38]), "oppositeDirection" : true, "depth" : 101.6 * mm});
        }
        {
            var Q0;
            {var subQ0=sQuery(id+"F0.wireOp",EDGE,"E12.0.16.0");var subQ1=sQuery(id+"F0.wireOp",EDGE,"E2.bottom");var subQ2=makeQuery(id+"F0.imprint","INTERSECT",VERTEX,{"derivedFrom":[subQ1,subQ0]});Q0=makeQuery(id+"F0.imprint","IMPRINT",FACE,{"disambiguationData":[TD([[makeQuery(id+"F0.imprint","IMPRINT",EDGE,{"disambiguationData":[TD([[subQ2,-1.0]])],"derivedFrom":subQ1}),1.0]])]});}
            var Q1;
            {var subQ0=sQuery(id+"F0.wireOp",EDGE,"E7.0.15.0");var subQ1=sQuery(id+"F0.wireOp",EDGE,"E2.bottom");var subQ2=makeQuery(id+"F0.imprint","INTERSECT",VERTEX,{"derivedFrom":[subQ1,subQ0]});Q1=makeQuery(id+"F0.imprint","IMPRINT",FACE,{"disambiguationData":[TD([[makeQuery(id+"F0.imprint","IMPRINT",EDGE,{"disambiguationData":[TD([[subQ2,-1.0]])],"derivedFrom":subQ1}),1.0]])]});}
            var Q2;
            {var subQ0=sQuery(id+"F0.wireOp",EDGE,"E7.0.14.0");var subQ1=sQuery(id+"F0.wireOp",EDGE,"E2.bottom");var subQ2=makeQuery(id+"F0.imprint","INTERSECT",VERTEX,{"derivedFrom":[subQ1,subQ0]});Q2=makeQuery(id+"F0.imprint","IMPRINT",FACE,{"disambiguationData":[TD([[makeQuery(id+"F0.imprint","IMPRINT",EDGE,{"disambiguationData":[TD([[subQ2,-1.0]])],"derivedFrom":subQ1}),1.0]])]});}
            var Q3;
            {var subQ0=sQuery(id+"F0.wireOp",EDGE,"E6.0.13.0");var subQ1=sQuery(id+"F0.wireOp",EDGE,"E2.bottom");var subQ2=makeQuery(id+"F0.imprint","INTERSECT",VERTEX,{"derivedFrom":[subQ1,subQ0]});Q3=makeQuery(id+"F0.imprint","IMPRINT",FACE,{"disambiguationData":[TD([[makeQuery(id+"F0.imprint","IMPRINT",EDGE,{"disambiguationData":[TD([[subQ2,-1.0]])],"derivedFrom":subQ1}),1.0]])]});}
            var Q4;
            {var subQ0=sQuery(id+"F0.wireOp",EDGE,"E6.0.12.0");var subQ1=sQuery(id+"F0.wireOp",EDGE,"E2.bottom");var subQ2=makeQuery(id+"F0.imprint","INTERSECT",VERTEX,{"derivedFrom":[subQ1,subQ0]});Q4=makeQuery(id+"F0.imprint","IMPRINT",FACE,{"disambiguationData":[TD([[makeQuery(id+"F0.imprint","IMPRINT",EDGE,{"disambiguationData":[TD([[subQ2,-1.0]])],"derivedFrom":subQ1}),1.0]])]});}
            var Q5;
            {var subQ0=sQuery(id+"F0.wireOp",EDGE,"E5.0.11.0");var subQ1=sQuery(id+"F0.wireOp",EDGE,"E2.bottom");var subQ2=makeQuery(id+"F0.imprint","INTERSECT",VERTEX,{"derivedFrom":[subQ1,subQ0]});Q5=makeQuery(id+"F0.imprint","IMPRINT",FACE,{"disambiguationData":[TD([[makeQuery(id+"F0.imprint","IMPRINT",EDGE,{"disambiguationData":[TD([[subQ2,-1.0]])],"derivedFrom":subQ1}),1.0]])]});}
            var Q6;
            {var subQ0=sQuery(id+"F0.wireOp",EDGE,"E5.0.10.0");var subQ1=sQuery(id+"F0.wireOp",EDGE,"E2.bottom");var subQ2=makeQuery(id+"F0.imprint","INTERSECT",VERTEX,{"derivedFrom":[subQ1,subQ0]});Q6=makeQuery(id+"F0.imprint","IMPRINT",FACE,{"disambiguationData":[TD([[makeQuery(id+"F0.imprint","IMPRINT",EDGE,{"disambiguationData":[TD([[subQ2,-1.0]])],"derivedFrom":subQ1}),1.0]])]});}
            var Q7;
            {var subQ0=sQuery(id+"F0.wireOp",EDGE,"E5.0.9.0");var subQ1=sQuery(id+"F0.wireOp",EDGE,"E2.bottom");var subQ2=makeQuery(id+"F0.imprint","INTERSECT",VERTEX,{"derivedFrom":[subQ1,subQ0]});Q7=makeQuery(id+"F0.imprint","IMPRINT",FACE,{"disambiguationData":[TD([[makeQuery(id+"F0.imprint","IMPRINT",EDGE,{"disambiguationData":[TD([[subQ2,-1.0]])],"derivedFrom":subQ1}),1.0]])]});}
            var Q8;
            {var subQ0=sQuery(id+"F0.wireOp",EDGE,"E5.0.8.0");var subQ1=sQuery(id+"F0.wireOp",EDGE,"E2.bottom");var subQ2=makeQuery(id+"F0.imprint","INTERSECT",VERTEX,{"derivedFrom":[subQ1,subQ0]});Q8=makeQuery(id+"F0.imprint","IMPRINT",FACE,{"disambiguationData":[TD([[makeQuery(id+"F0.imprint","IMPRINT",EDGE,{"disambiguationData":[TD([[subQ2,-1.0]])],"derivedFrom":subQ1}),1.0]])]});}
            var Q9;
            {var subQ0=sQuery(id+"F0.wireOp",EDGE,"E5.0.7.0");var subQ1=sQuery(id+"F0.wireOp",EDGE,"E2.bottom");var subQ2=makeQuery(id+"F0.imprint","INTERSECT",VERTEX,{"derivedFrom":[subQ1,subQ0]});Q9=makeQuery(id+"F0.imprint","IMPRINT",FACE,{"disambiguationData":[TD([[makeQuery(id+"F0.imprint","IMPRINT",EDGE,{"disambiguationData":[TD([[subQ2,-1.0]])],"derivedFrom":subQ1}),1.0]])]});}
            var Q10;
            {var subQ0=sQuery(id+"F0.wireOp",EDGE,"E5.0.6.0");var subQ1=sQuery(id+"F0.wireOp",EDGE,"E2.bottom");var subQ2=makeQuery(id+"F0.imprint","INTERSECT",VERTEX,{"derivedFrom":[subQ1,subQ0]});Q10=makeQuery(id+"F0.imprint","IMPRINT",FACE,{"disambiguationData":[TD([[makeQuery(id+"F0.imprint","IMPRINT",EDGE,{"disambiguationData":[TD([[subQ2,-1.0]])],"derivedFrom":subQ1}),1.0]])]});}
            var Q11;
            {var subQ0=sQuery(id+"F0.wireOp",EDGE,"E5.0.5.0");var subQ1=sQuery(id+"F0.wireOp",EDGE,"E2.bottom");var subQ2=makeQuery(id+"F0.imprint","INTERSECT",VERTEX,{"derivedFrom":[subQ1,subQ0]});Q11=makeQuery(id+"F0.imprint","IMPRINT",FACE,{"disambiguationData":[TD([[makeQuery(id+"F0.imprint","IMPRINT",EDGE,{"disambiguationData":[TD([[subQ2,-1.0]])],"derivedFrom":subQ1}),1.0]])]});}
            var Q12;
            {var subQ0=sQuery(id+"F0.wireOp",EDGE,"E5.0.4.0");var subQ1=sQuery(id+"F0.wireOp",EDGE,"E2.bottom");var subQ2=makeQuery(id+"F0.imprint","INTERSECT",VERTEX,{"derivedFrom":[subQ1,subQ0]});Q12=makeQuery(id+"F0.imprint","IMPRINT",FACE,{"disambiguationData":[TD([[makeQuery(id+"F0.imprint","IMPRINT",EDGE,{"disambiguationData":[TD([[subQ2,-1.0]])],"derivedFrom":subQ1}),1.0]])]});}
            var Q13;
            {var subQ0=sQuery(id+"F0.wireOp",EDGE,"E5.0.3.0");var subQ1=sQuery(id+"F0.wireOp",EDGE,"E2.bottom");var subQ2=makeQuery(id+"F0.imprint","INTERSECT",VERTEX,{"derivedFrom":[subQ1,subQ0]});Q13=makeQuery(id+"F0.imprint","IMPRINT",FACE,{"disambiguationData":[TD([[makeQuery(id+"F0.imprint","IMPRINT",EDGE,{"disambiguationData":[TD([[subQ2,-1.0]])],"derivedFrom":subQ1}),1.0]])]});}
            var Q14;
            {var subQ0=sQuery(id+"F0.wireOp",EDGE,"E4.2.0.0");var subQ1=sQuery(id+"F0.wireOp",EDGE,"E2.bottom");var subQ2=makeQuery(id+"F0.imprint","INTERSECT",VERTEX,{"derivedFrom":[subQ1,subQ0]});Q14=makeQuery(id+"F0.imprint","IMPRINT",FACE,{"disambiguationData":[TD([[makeQuery(id+"F0.imprint","IMPRINT",EDGE,{"disambiguationData":[TD([[subQ2,-1.0]])],"derivedFrom":subQ1}),1.0]])]});}
            var Q15;
            {var subQ0=sQuery(id+"F0.wireOp",EDGE,"E4.1.0.0");var subQ1=sQuery(id+"F0.wireOp",EDGE,"E2.bottom");var subQ2=makeQuery(id+"F0.imprint","INTERSECT",VERTEX,{"derivedFrom":[subQ1,subQ0]});Q15=makeQuery(id+"F0.imprint","IMPRINT",FACE,{"disambiguationData":[TD([[makeQuery(id+"F0.imprint","IMPRINT",EDGE,{"disambiguationData":[TD([[subQ2,-1.0]])],"derivedFrom":subQ1}),1.0]])]});}
            var Q16;
            {var subQ0=sQuery(id+"F0.wireOp",EDGE,"E3.right");var subQ1=sQuery(id+"F0.wireOp",EDGE,"E2.bottom");var subQ2=makeQuery(id+"F0.imprint","INTERSECT",VERTEX,{"derivedFrom":[subQ1,subQ0]});Q16=makeQuery(id+"F0.imprint","IMPRINT",FACE,{"disambiguationData":[TD([[makeQuery(id+"F0.imprint","IMPRINT",EDGE,{"disambiguationData":[TD([[subQ2,-1.0]])],"derivedFrom":subQ1}),1.0]])]});}
            extrude(context, id + "F5", {"entities" : qUnion([Q0, Q1, Q2, Q3, Q4, Q5, Q6, Q7, Q8, Q9, Q10, Q11, Q12, Q13, Q14, Q15, Q16]), "operationType" : NewBodyOperationType.REMOVE, "oppositeDirection" : true, "depth" : 50.8 * mm});
        }
    });
